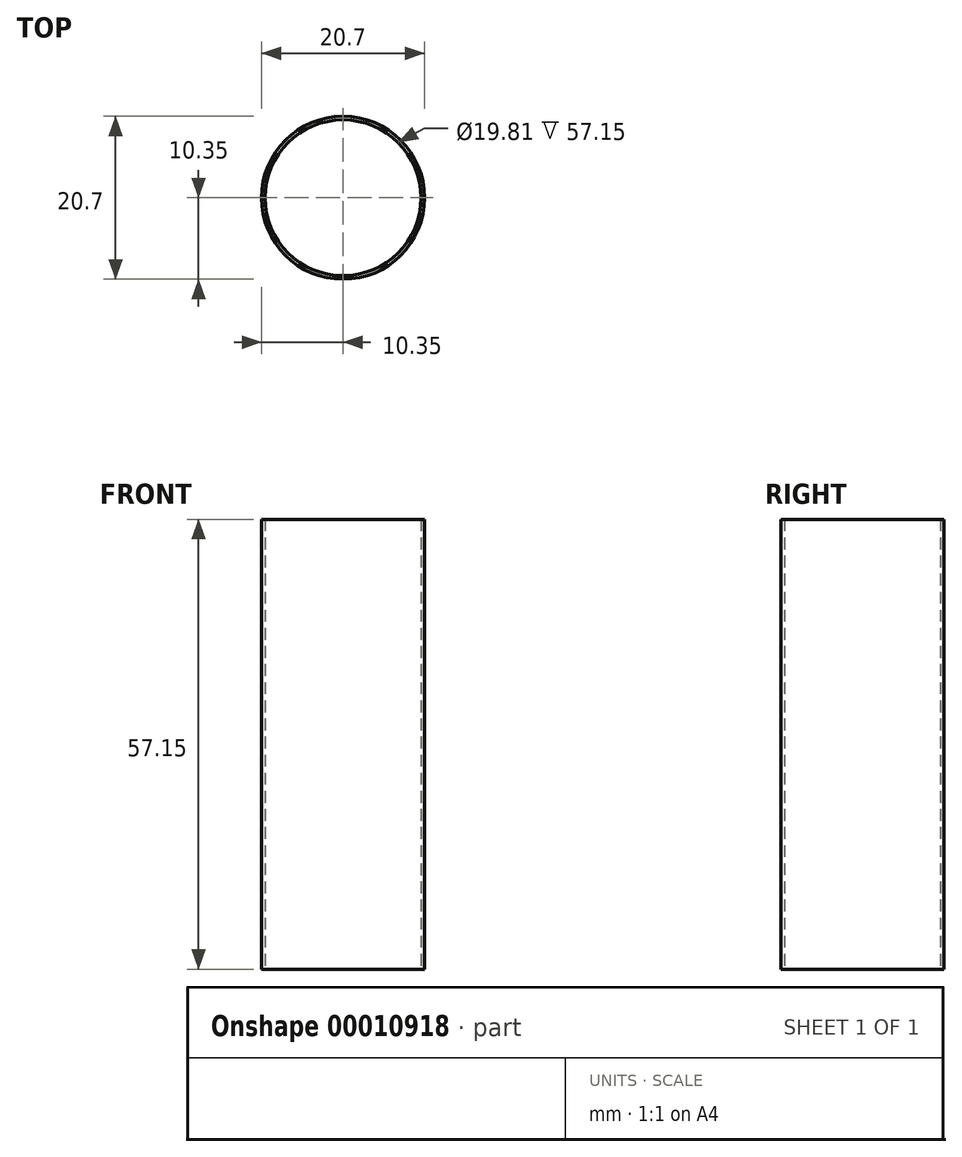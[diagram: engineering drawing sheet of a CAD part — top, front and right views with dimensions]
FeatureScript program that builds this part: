
annotation { "Feature Type Name" : "Feature", "Feature Type Description" : "" }
export const myFeature = defineFeature(function(context is Context, id is Id, definition is map)
    precondition{}
    {
        {
            var Q0;
            Q0=qCreatedBy(makeId("Top.planeOp"),FACE);
            var sketch = newSketch(context, id + "F0", { "sketchPlane" : qUnion([Q0])});
            skCircle(sketch, "E0", {"center": v(0, 0) * mm, "radius": 10.35 * mm});
            skCircle(sketch, "E1", {"center": v(0, 0) * mm, "radius": 9.9 * mm});
            skSolve(sketch);
        }
        {
            var Q0;
            Q0=makeQuery(id+"F0.imprint","IMPRINT",FACE,{"disambiguationData":[TD([[makeQuery(id+"F0.imprint","IMPRINT",EDGE,{"derivedFrom":sQuery(id+"F0.wireOp",EDGE,"E0")}),1.0]])]});
            extrude(context, id + "F1", {"entities" : qUnion([Q0]), "depth" : 57.15 * mm});
        }
    });
